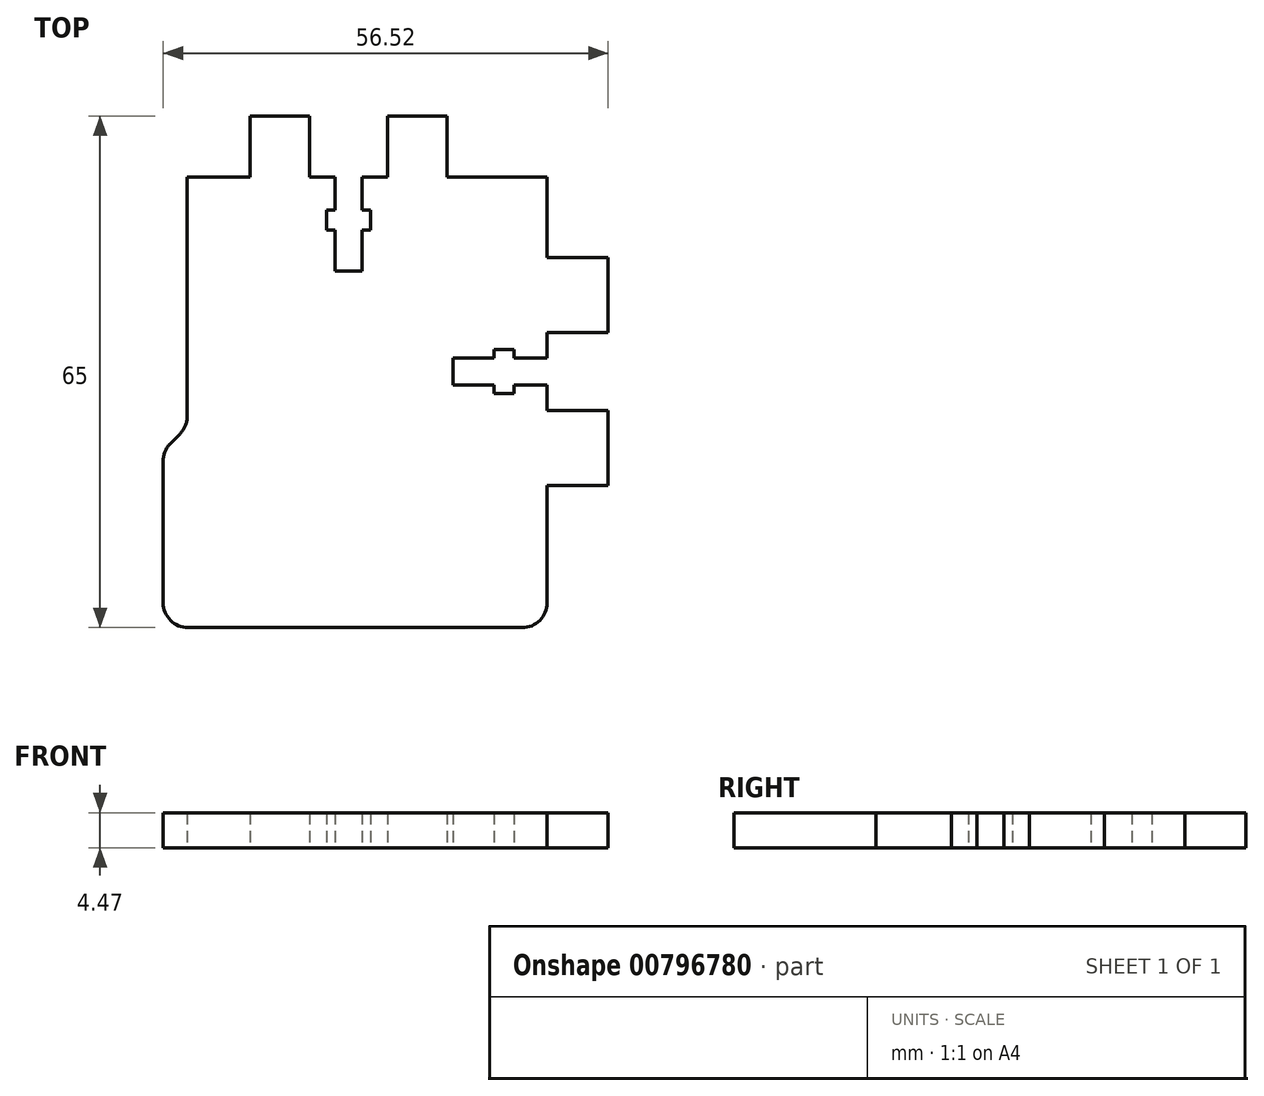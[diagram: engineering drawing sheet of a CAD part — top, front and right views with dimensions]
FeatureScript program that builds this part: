
annotation { "Feature Type Name" : "Feature", "Feature Type Description" : "" }
export const myFeature = defineFeature(function(context is Context, id is Id, definition is map)
    precondition{}
    {
        {
            var Q0;
            Q0=qCreatedBy(makeId("Top.planeOp"),FACE);
            var sketch = newSketch(context, id + "F0", { "sketchPlane" : qUnion([Q0])});
            skLineSegment(sketch, "E0", {"start": v(0, 69.32) * mm, "end": v(0, 0) * mm, "construction": true});
            skLineSegment(sketch, "E1", {"start": v(0, 0) * mm, "end": v(87.96, 0) * mm, "construction": true});
            skLineSegment(sketch, "E2", {"start": v(0, 3.18) * mm, "end": v(0, 21.16) * mm});
            skLineSegment(sketch, "E3", {"start": v(0.93, 23.4) * mm, "end": v(2.12, 24.6) * mm});
            skLineSegment(sketch, "E4", {"start": v(3.05, 26.84) * mm, "end": v(3.05, 57.25) * mm});
            skLineSegment(sketch, "E5", {"start": v(3.05, 57.25) * mm, "end": v(11.05, 57.25) * mm});
            skLineSegment(sketch, "E6", {"start": v(11.05, 57.25) * mm, "end": v(11.05, 65) * mm});
            skLineSegment(sketch, "E7", {"start": v(11.05, 65) * mm, "end": v(18.6, 65) * mm});
            skLineSegment(sketch, "E8", {"start": v(18.6, 65) * mm, "end": v(18.6, 57.25) * mm});
            skLineSegment(sketch, "E9", {"start": v(18.6, 57.25) * mm, "end": v(21.84, 57.25) * mm});
            skLineSegment(sketch, "E10", {"start": v(21.84, 57.25) * mm, "end": v(21.84, 53.06) * mm});
            skLineSegment(sketch, "E11", {"start": v(21.84, 53.06) * mm, "end": v(20.76, 53.06) * mm});
            skLineSegment(sketch, "E12", {"start": v(20.76, 53.06) * mm, "end": v(20.76, 50.52) * mm});
            skLineSegment(sketch, "E13", {"start": v(20.76, 50.52) * mm, "end": v(21.84, 50.52) * mm});
            skLineSegment(sketch, "E14", {"start": v(21.84, 50.52) * mm, "end": v(21.84, 45.31) * mm});
            skLineSegment(sketch, "E15", {"start": v(21.84, 45.31) * mm, "end": v(25.27, 45.31) * mm});
            skLineSegment(sketch, "E16", {"start": v(25.27, 45.31) * mm, "end": v(25.27, 50.52) * mm});
            skLineSegment(sketch, "E17", {"start": v(25.27, 50.52) * mm, "end": v(26.35, 50.52) * mm});
            skLineSegment(sketch, "E18", {"start": v(26.35, 50.52) * mm, "end": v(26.35, 53.06) * mm});
            skLineSegment(sketch, "E19", {"start": v(26.35, 53.06) * mm, "end": v(25.27, 53.06) * mm});
            skLineSegment(sketch, "E20", {"start": v(25.27, 53.06) * mm, "end": v(25.27, 57.25) * mm});
            skLineSegment(sketch, "E21", {"start": v(25.27, 57.25) * mm, "end": v(28.52, 57.25) * mm});
            skLineSegment(sketch, "E22", {"start": v(28.52, 57.25) * mm, "end": v(28.52, 65) * mm});
            skLineSegment(sketch, "E23", {"start": v(28.52, 65) * mm, "end": v(36.07, 65) * mm});
            skLineSegment(sketch, "E24", {"start": v(36.07, 65) * mm, "end": v(36.07, 57.25) * mm});
            skLineSegment(sketch, "E25", {"start": v(36.07, 57.25) * mm, "end": v(48.77, 57.25) * mm});
            skLineSegment(sketch, "E26", {"start": v(48.77, 57.25) * mm, "end": v(48.77, 47.04) * mm});
            skLineSegment(sketch, "E27", {"start": v(48.77, 47.04) * mm, "end": v(56.52, 47.04) * mm});
            skLineSegment(sketch, "E28", {"start": v(56.52, 47.04) * mm, "end": v(56.52, 37.5) * mm});
            skLineSegment(sketch, "E29", {"start": v(56.52, 37.5) * mm, "end": v(48.77, 37.5) * mm});
            skLineSegment(sketch, "E30", {"start": v(48.77, 37.5) * mm, "end": v(48.77, 34.25) * mm});
            skLineSegment(sketch, "E31", {"start": v(48.77, 34.25) * mm, "end": v(44.58, 34.25) * mm});
            skLineSegment(sketch, "E32", {"start": v(44.58, 34.25) * mm, "end": v(44.58, 35.33) * mm});
            skLineSegment(sketch, "E33", {"start": v(44.58, 35.33) * mm, "end": v(42.04, 35.33) * mm});
            skLineSegment(sketch, "E34", {"start": v(42.04, 35.33) * mm, "end": v(42.04, 34.25) * mm});
            skLineSegment(sketch, "E35", {"start": v(42.04, 34.25) * mm, "end": v(36.83, 34.25) * mm});
            skLineSegment(sketch, "E36", {"start": v(36.83, 34.25) * mm, "end": v(36.83, 30.82) * mm});
            skLineSegment(sketch, "E37", {"start": v(36.83, 30.82) * mm, "end": v(42.04, 30.82) * mm});
            skLineSegment(sketch, "E38", {"start": v(42.04, 30.82) * mm, "end": v(42.04, 29.74) * mm});
            skLineSegment(sketch, "E39", {"start": v(42.04, 29.74) * mm, "end": v(44.58, 29.74) * mm});
            skLineSegment(sketch, "E40", {"start": v(44.58, 29.74) * mm, "end": v(44.58, 30.82) * mm});
            skLineSegment(sketch, "E41", {"start": v(44.58, 30.82) * mm, "end": v(48.77, 30.82) * mm});
            skLineSegment(sketch, "E42", {"start": v(48.77, 30.82) * mm, "end": v(48.77, 27.58) * mm});
            skLineSegment(sketch, "E43", {"start": v(48.77, 27.58) * mm, "end": v(56.52, 27.58) * mm});
            skLineSegment(sketch, "E44", {"start": v(56.52, 27.58) * mm, "end": v(56.52, 18.03) * mm});
            skLineSegment(sketch, "E45", {"start": v(56.52, 18.03) * mm, "end": v(48.77, 18.03) * mm});
            skLineSegment(sketch, "E46", {"start": v(48.77, 18.03) * mm, "end": v(48.77, 3.17) * mm});
            skLineSegment(sketch, "E47", {"start": v(45.6, 0) * mm, "end": v(3.17, 0) * mm});
            skLineSegment(sketch, "E48", {"start": v(23.56, 61.35) * mm, "end": v(23.56, 32.54) * mm, "construction": true});
            skLineSegment(sketch, "E49", {"start": v(23.56, 32.54) * mm, "end": v(74.38, 32.54) * mm, "construction": true});
            skLineSegment(sketch, "E50", {"start": v(15.56, 51.8) * mm, "end": v(31.57, 51.8) * mm, "construction": true});
            skLineSegment(sketch, "E51", {"start": v(43.3, 42.12) * mm, "end": v(43.3, 17.26) * mm, "construction": true});
            skPoint(sketch, "E52.visualSharp", {"position": v(3.05, 25.53) * mm});
            skArc(sketch, "E52.filletArc", {"start": v(2.12, 24.6) * mm, "mid": v(2.8, 25.63) * mm, "end": v(3.05, 26.84) * mm});
            skPoint(sketch, "E53.visualSharp", {"position": v(0, 22.48) * mm});
            skArc(sketch, "E53.filletArc", {"start": v(0.93, 23.4) * mm, "mid": v(0.24, 22.38) * mm, "end": v(0, 21.16) * mm});
            skPoint(sketch, "E54.visualSharp", {"position": v(0, 0) * mm});
            skArc(sketch, "E54.filletArc", {"start": v(0, 3.17) * mm, "mid": v(0.93, 0.93) * mm, "end": v(3.17, 0) * mm});
            skPoint(sketch, "E55.visualSharp", {"position": v(48.77, 0) * mm});
            skArc(sketch, "E55.filletArc", {"start": v(45.6, 0) * mm, "mid": v(47.84, 0.93) * mm, "end": v(48.77, 3.17) * mm});
            skSolve(sketch);
        }
        {
            var Q0;
            Q0=makeQuery(id+"F0.imprint","IMPRINT",FACE,{"disambiguationData":[TD([[makeQuery(id+"F0.imprint","IMPRINT",EDGE,{"derivedFrom":sQuery(id+"F0.wireOp",EDGE,"E2")}),-1.0]])]});
            extrude(context, id + "F1", {"entities" : qUnion([Q0]), "depth" : 4.47 * mm, "offsetDistance" : 25.4 * mm});
        }
    });
